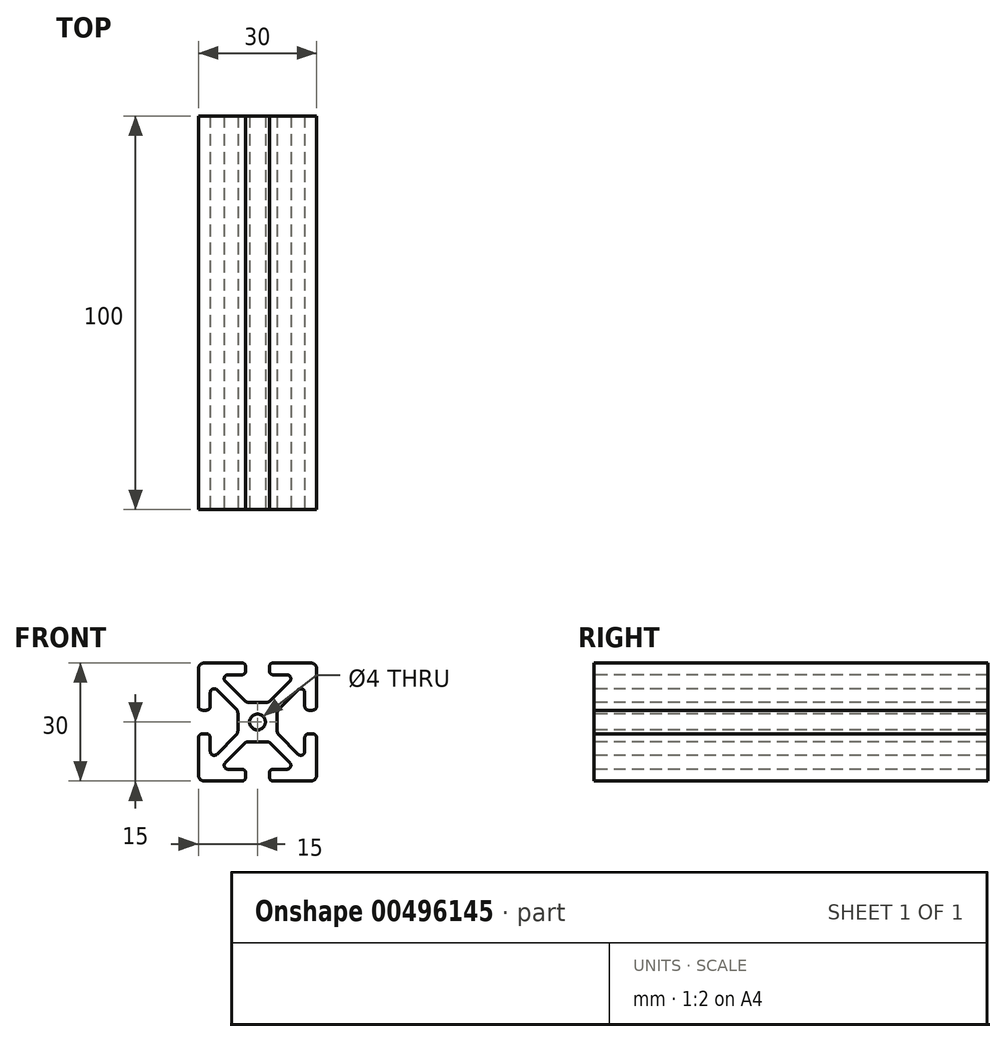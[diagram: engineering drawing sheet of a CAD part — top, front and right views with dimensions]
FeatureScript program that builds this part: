
annotation { "Feature Type Name" : "Feature", "Feature Type Description" : "" }
export const myFeature = defineFeature(function(context is Context, id is Id, definition is map)
    precondition{}
    {
        {
            var Q0;
            Q0=qCreatedBy(makeId("Front.planeOp"),FACE);
            var sketch = newSketch(context, id + "F0", { "sketchPlane" : qUnion([Q0])});
            skLineSegment(sketch, "E0.bottom", {"start": v(13.5, 15) * mm, "end": v(4, 15) * mm});
            skLineSegment(sketch, "E0.top", {"start": v(13.5, -15) * mm, "end": v(4, -15) * mm});
            skLineSegment(sketch, "E0.left", {"start": v(15, 13.5) * mm, "end": v(15, 4) * mm});
            skLineSegment(sketch, "E0.right", {"start": v(-15, 13.5) * mm, "end": v(-15, 4) * mm});
            skPoint(sketch, "E0.middle", {"position": v(0, 0) * mm});
            skLineSegment(sketch, "E1.bottom", {"start": v(7.46, 12) * mm, "end": v(4, 12) * mm});
            skLineSegment(sketch, "E1.top", {"start": v(7.46, -12) * mm, "end": v(4, -12) * mm});
            skLineSegment(sketch, "E1.left", {"start": v(12, 7.46) * mm, "end": v(12, 4) * mm});
            skLineSegment(sketch, "E1.right", {"start": v(-12, 7.46) * mm, "end": v(-12, 4) * mm});
            skLineSegment(sketch, "E2", {"start": v(8.17, 10.3) * mm, "end": v(3.32, 5.44) * mm});
            skLineSegment(sketch, "E3", {"start": v(-8.17, -10.3) * mm, "end": v(-3.32, -5.44) * mm});
            skLineSegment(sketch, "E4", {"start": v(-8.17, 10.3) * mm, "end": v(-3.32, 5.44) * mm});
            skLineSegment(sketch, "E5", {"start": v(-10.3, 8.17) * mm, "end": v(-5.44, 3.32) * mm});
            skPoint(sketch, "E6.orphan", {"position": v(12, 12) * mm});
            skPoint(sketch, "E7.orphan", {"position": v(12, -12) * mm});
            skPoint(sketch, "E8.orphan", {"position": v(-12, -12) * mm});
            skPoint(sketch, "E9.orphan", {"position": v(-12, 12) * mm});
            skLineSegment(sketch, "E10.trimOffspring", {"start": v(-5.44, -3.32) * mm, "end": v(-10.3, -8.17) * mm});
            skLineSegment(sketch, "E11.trimOffspring", {"start": v(5.44, -3.32) * mm, "end": v(10.3, -8.17) * mm});
            skLineSegment(sketch, "E12.trimOffspring", {"start": v(5.44, 3.32) * mm, "end": v(10.3, 8.17) * mm});
            skLineSegment(sketch, "E13.trimOffspring", {"start": v(3.32, -5.44) * mm, "end": v(8.17, -10.3) * mm});
            skLineSegment(sketch, "E14.bottom", {"start": v(2.26, 5) * mm, "end": v(-2.26, 5) * mm});
            skLineSegment(sketch, "E14.top", {"start": v(2.26, -5) * mm, "end": v(-2.26, -5) * mm});
            skLineSegment(sketch, "E14.left", {"start": v(5, 2.26) * mm, "end": v(5, -2.26) * mm});
            skLineSegment(sketch, "E14.right", {"start": v(-5, 2.26) * mm, "end": v(-5, -2.26) * mm});
            skPoint(sketch, "E15.orphan", {"position": v(5, 5) * mm});
            skPoint(sketch, "E16.orphan", {"position": v(5, -5) * mm});
            skPoint(sketch, "E17.orphan", {"position": v(-5, -5) * mm});
            skPoint(sketch, "E18.orphan", {"position": v(-5, 5) * mm});
            skCircle(sketch, "E19", {"center": v(0, 0) * mm, "radius": 2 * mm});
            skLineSegment(sketch, "E20", {"start": v(-3, 14) * mm, "end": v(-3, 13) * mm});
            skLineSegment(sketch, "E21", {"start": v(3, 14) * mm, "end": v(3, 13) * mm});
            skLineSegment(sketch, "E22.trimOffspring", {"start": v(-3, -13) * mm, "end": v(-3, -14) * mm});
            skLineSegment(sketch, "E23.trimOffspring", {"start": v(-4, 12) * mm, "end": v(-7.46, 12) * mm});
            skLineSegment(sketch, "E24.trimOffspring", {"start": v(-4, 15) * mm, "end": v(-13.5, 15) * mm});
            skLineSegment(sketch, "E25.trimOffspring", {"start": v(3, -13) * mm, "end": v(3, -14) * mm});
            skLineSegment(sketch, "E26.trimOffspring", {"start": v(-4, -12) * mm, "end": v(-7.46, -12) * mm});
            skLineSegment(sketch, "E27.trimOffspring", {"start": v(-4, -15) * mm, "end": v(-13.5, -15) * mm});
            skLineSegment(sketch, "E28", {"start": v(-14, 3) * mm, "end": v(-13, 3) * mm});
            skLineSegment(sketch, "E29", {"start": v(-14, -3) * mm, "end": v(-13, -3) * mm});
            skLineSegment(sketch, "E30.trimOffspring", {"start": v(-12, -4) * mm, "end": v(-12, -7.46) * mm});
            skLineSegment(sketch, "E31.trimOffspring", {"start": v(-15, -4) * mm, "end": v(-15, -13.5) * mm});
            skLineSegment(sketch, "E32.trimOffspring", {"start": v(13, 3) * mm, "end": v(14, 3) * mm});
            skLineSegment(sketch, "E33.trimOffspring", {"start": v(13, -3) * mm, "end": v(14, -3) * mm});
            skLineSegment(sketch, "E34.trimOffspring", {"start": v(12, -4) * mm, "end": v(12, -7.46) * mm});
            skLineSegment(sketch, "E35.trimOffspring", {"start": v(15, -4) * mm, "end": v(15, -13.5) * mm});
            skPoint(sketch, "E36.visualSharp", {"position": v(-15, 15) * mm});
            skArc(sketch, "E36.filletArc", {"start": v(-13.5, 15) * mm, "mid": v(-14.56, 14.56) * mm, "end": v(-15, 13.5) * mm});
            skPoint(sketch, "E37.visualSharp", {"position": v(15, 15) * mm});
            skArc(sketch, "E37.filletArc", {"start": v(15, 13.5) * mm, "mid": v(14.56, 14.56) * mm, "end": v(13.5, 15) * mm});
            skPoint(sketch, "E38.visualSharp", {"position": v(15, -15) * mm});
            skArc(sketch, "E38.filletArc", {"start": v(13.5, -15) * mm, "mid": v(14.56, -14.56) * mm, "end": v(15, -13.5) * mm});
            skPoint(sketch, "E39.visualSharp", {"position": v(-15, -15) * mm});
            skArc(sketch, "E39.filletArc", {"start": v(-15, -13.5) * mm, "mid": v(-14.56, -14.56) * mm, "end": v(-13.5, -15) * mm});
            skPoint(sketch, "E40.visualSharp", {"position": v(-5, -2.88) * mm});
            skArc(sketch, "E40.filletArc", {"start": v(-5.44, -3.32) * mm, "mid": v(-5.11, -2.83) * mm, "end": v(-5, -2.26) * mm});
            skPoint(sketch, "E41.visualSharp", {"position": v(-2.88, -5) * mm});
            skArc(sketch, "E41.filletArc", {"start": v(-2.26, -5) * mm, "mid": v(-2.83, -5.11) * mm, "end": v(-3.32, -5.44) * mm});
            skPoint(sketch, "E42.visualSharp", {"position": v(2.88, -5) * mm});
            skArc(sketch, "E42.filletArc", {"start": v(3.32, -5.44) * mm, "mid": v(2.83, -5.11) * mm, "end": v(2.26, -5) * mm});
            skPoint(sketch, "E43.visualSharp", {"position": v(5, -2.88) * mm});
            skArc(sketch, "E43.filletArc", {"start": v(5, -2.26) * mm, "mid": v(5.11, -2.83) * mm, "end": v(5.44, -3.32) * mm});
            skPoint(sketch, "E44.visualSharp", {"position": v(5, 2.88) * mm});
            skArc(sketch, "E44.filletArc", {"start": v(5.44, 3.32) * mm, "mid": v(5.11, 2.83) * mm, "end": v(5, 2.26) * mm});
            skPoint(sketch, "E45.visualSharp", {"position": v(2.88, 5) * mm});
            skArc(sketch, "E45.filletArc", {"start": v(2.26, 5) * mm, "mid": v(2.83, 5.11) * mm, "end": v(3.32, 5.44) * mm});
            skPoint(sketch, "E46.visualSharp", {"position": v(-2.88, 5) * mm});
            skArc(sketch, "E46.filletArc", {"start": v(-3.32, 5.44) * mm, "mid": v(-2.83, 5.11) * mm, "end": v(-2.26, 5) * mm});
            skPoint(sketch, "E47.visualSharp", {"position": v(-3, 12) * mm});
            skArc(sketch, "E47.filletArc", {"start": v(-4, 12) * mm, "mid": v(-3.3, 12.3) * mm, "end": v(-3, 13) * mm});
            skPoint(sketch, "E48.visualSharp", {"position": v(-3, 15) * mm});
            skArc(sketch, "E48.filletArc", {"start": v(-3, 14) * mm, "mid": v(-3.3, 14.7) * mm, "end": v(-4, 15) * mm});
            skPoint(sketch, "E49.visualSharp", {"position": v(3, 15) * mm});
            skArc(sketch, "E49.filletArc", {"start": v(4, 15) * mm, "mid": v(3.3, 14.7) * mm, "end": v(3, 14) * mm});
            skPoint(sketch, "E50.visualSharp", {"position": v(3, 12) * mm});
            skArc(sketch, "E50.filletArc", {"start": v(3, 13) * mm, "mid": v(3.3, 12.3) * mm, "end": v(4, 12) * mm});
            skPoint(sketch, "E51.visualSharp", {"position": v(12, 3) * mm});
            skArc(sketch, "E51.filletArc", {"start": v(12, 4) * mm, "mid": v(12.3, 3.3) * mm, "end": v(13, 3) * mm});
            skPoint(sketch, "E52.visualSharp", {"position": v(15, 3) * mm});
            skArc(sketch, "E52.filletArc", {"start": v(14, 3) * mm, "mid": v(14.7, 3.3) * mm, "end": v(15, 4) * mm});
            skPoint(sketch, "E53.visualSharp", {"position": v(15, -3) * mm});
            skArc(sketch, "E53.filletArc", {"start": v(15, -4) * mm, "mid": v(14.7, -3.3) * mm, "end": v(14, -3) * mm});
            skPoint(sketch, "E54.visualSharp", {"position": v(12, -3) * mm});
            skArc(sketch, "E54.filletArc", {"start": v(13, -3) * mm, "mid": v(12.3, -3.3) * mm, "end": v(12, -4) * mm});
            skPoint(sketch, "E55.visualSharp", {"position": v(3, -12) * mm});
            skArc(sketch, "E55.filletArc", {"start": v(4, -12) * mm, "mid": v(3.3, -12.3) * mm, "end": v(3, -13) * mm});
            skPoint(sketch, "E56.visualSharp", {"position": v(3, -15) * mm});
            skArc(sketch, "E56.filletArc", {"start": v(3, -14) * mm, "mid": v(3.3, -14.7) * mm, "end": v(4, -15) * mm});
            skPoint(sketch, "E57.visualSharp", {"position": v(-3, -12) * mm});
            skArc(sketch, "E57.filletArc", {"start": v(-3, -13) * mm, "mid": v(-3.3, -12.3) * mm, "end": v(-4, -12) * mm});
            skPoint(sketch, "E58.visualSharp", {"position": v(-3, -15) * mm});
            skArc(sketch, "E58.filletArc", {"start": v(-4, -15) * mm, "mid": v(-3.3, -14.7) * mm, "end": v(-3, -14) * mm});
            skPoint(sketch, "E59.visualSharp", {"position": v(-12, -3) * mm});
            skArc(sketch, "E59.filletArc", {"start": v(-12, -4) * mm, "mid": v(-12.3, -3.3) * mm, "end": v(-13, -3) * mm});
            skPoint(sketch, "E60.visualSharp", {"position": v(-15, -3) * mm});
            skArc(sketch, "E60.filletArc", {"start": v(-14, -3) * mm, "mid": v(-14.7, -3.3) * mm, "end": v(-15, -4) * mm});
            skPoint(sketch, "E61.visualSharp", {"position": v(-15, 3) * mm});
            skArc(sketch, "E61.filletArc", {"start": v(-15, 4) * mm, "mid": v(-14.7, 3.3) * mm, "end": v(-14, 3) * mm});
            skPoint(sketch, "E62.visualSharp", {"position": v(-12, 3) * mm});
            skArc(sketch, "E62.filletArc", {"start": v(-13, 3) * mm, "mid": v(-12.3, 3.3) * mm, "end": v(-12, 4) * mm});
            skPoint(sketch, "E63.visualSharp", {"position": v(9.88, 12) * mm});
            skArc(sketch, "E63.filletArc", {"start": v(8.17, 10.3) * mm, "mid": v(8.39, 11.38) * mm, "end": v(7.46, 12) * mm});
            skPoint(sketch, "E64.visualSharp", {"position": v(12, 9.88) * mm});
            skArc(sketch, "E64.filletArc", {"start": v(12, 7.46) * mm, "mid": v(11.38, 8.39) * mm, "end": v(10.3, 8.17) * mm});
            skPoint(sketch, "E65.visualSharp", {"position": v(12, -9.88) * mm});
            skArc(sketch, "E65.filletArc", {"start": v(10.3, -8.17) * mm, "mid": v(11.38, -8.39) * mm, "end": v(12, -7.46) * mm});
            skPoint(sketch, "E66.visualSharp", {"position": v(9.88, -12) * mm});
            skArc(sketch, "E66.filletArc", {"start": v(7.46, -12) * mm, "mid": v(8.39, -11.38) * mm, "end": v(8.17, -10.3) * mm});
            skPoint(sketch, "E67.visualSharp", {"position": v(-12, -9.88) * mm});
            skArc(sketch, "E67.filletArc", {"start": v(-12, -7.46) * mm, "mid": v(-11.38, -8.39) * mm, "end": v(-10.3, -8.17) * mm});
            skPoint(sketch, "E68.visualSharp", {"position": v(-9.88, -12) * mm});
            skArc(sketch, "E68.filletArc", {"start": v(-8.17, -10.3) * mm, "mid": v(-8.39, -11.38) * mm, "end": v(-7.46, -12) * mm});
            skPoint(sketch, "E69.visualSharp", {"position": v(-12, 9.88) * mm});
            skArc(sketch, "E69.filletArc", {"start": v(-10.3, 8.17) * mm, "mid": v(-11.38, 8.39) * mm, "end": v(-12, 7.46) * mm});
            skPoint(sketch, "E70.visualSharp", {"position": v(-9.88, 12) * mm});
            skArc(sketch, "E70.filletArc", {"start": v(-7.46, 12) * mm, "mid": v(-8.39, 11.38) * mm, "end": v(-8.17, 10.3) * mm});
            skPoint(sketch, "E71.visualSharp", {"position": v(-5, 2.88) * mm});
            skArc(sketch, "E71.filletArc", {"start": v(-5, 2.26) * mm, "mid": v(-5.11, 2.83) * mm, "end": v(-5.44, 3.32) * mm});
            skSolve(sketch);
        }
        {
            var Q0;
            Q0=qSketchRegion(id+"F0",true);
            extrude(context, id + "F1", {"entities" : qUnion([Q0]), "oppositeDirection" : true, "depth" : 100 * mm});
        }
    });
